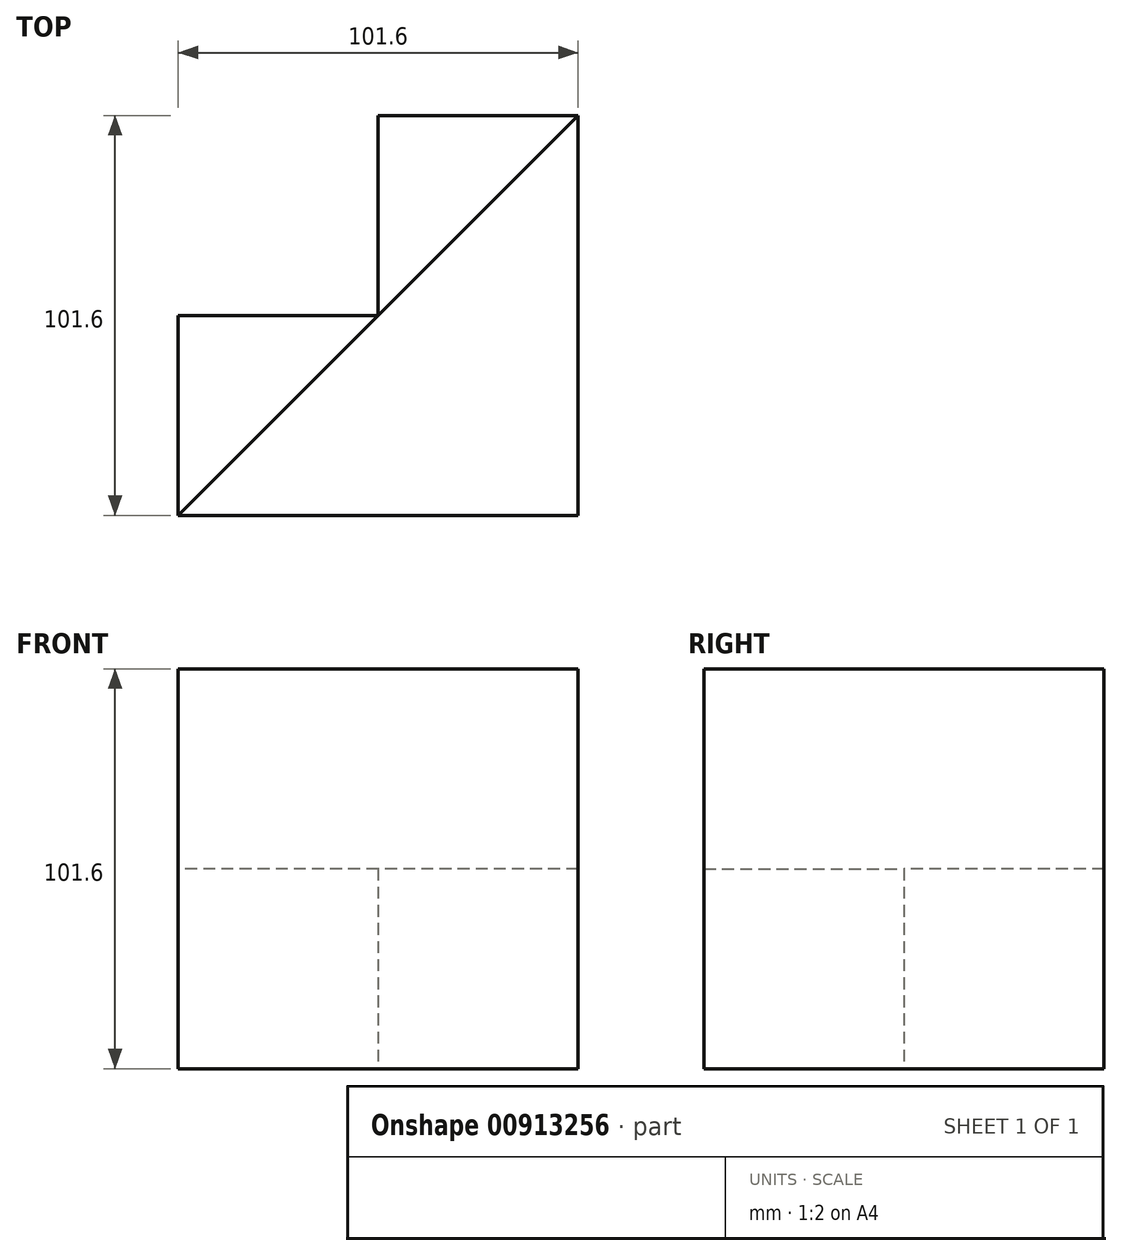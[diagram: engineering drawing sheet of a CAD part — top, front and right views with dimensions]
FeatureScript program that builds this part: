
annotation { "Feature Type Name" : "Feature", "Feature Type Description" : "" }
export const myFeature = defineFeature(function(context is Context, id is Id, definition is map)
    precondition{}
    {
        {
            var Q0;
            Q0=qCreatedBy(makeId("Top.planeOp"),FACE);
            var sketch = newSketch(context, id + "F0", { "sketchPlane" : qUnion([Q0])});
            skLineSegment(sketch, "E0.bottom", {"start": v(0, 0) * mm, "end": v(-101.6, 0) * mm});
            skLineSegment(sketch, "E0.top", {"start": v(0, 101.6) * mm, "end": v(-101.6, 101.6) * mm});
            skLineSegment(sketch, "E0.left", {"start": v(0, 0) * mm, "end": v(0, 101.6) * mm});
            skLineSegment(sketch, "E0.right", {"start": v(-101.6, 0) * mm, "end": v(-101.6, 101.6) * mm});
            skLineSegment(sketch, "E1", {"start": v(0, 101.6) * mm, "end": v(-101.6, 0) * mm});
            skSolve(sketch);
        }
        {
            var Q0;
            Q0=makeQuery(id+"F0.imprint","IMPRINT",FACE,{"disambiguationData":[TD([[makeQuery(id+"F0.imprint","IMPRINT",EDGE,{"derivedFrom":sQuery(id+"F0.wireOp",EDGE,"E0.bottom")}),-1.0]])]});
            extrude(context, id + "F1", {"entities" : qUnion([Q0]), "depth" : 101.6 * mm, "offsetDistance" : 25.4 * mm});
        }
        {
            var Q0;
            Q0=qCreatedBy(makeId("Top.planeOp"),FACE);
            var sketch = newSketch(context, id + "F2", { "sketchPlane" : qUnion([Q0])});
            skLineSegment(sketch, "E2.bottom", {"start": v(0, 0) * mm, "end": v(-101.6, 0) * mm});
            skLineSegment(sketch, "E2.top", {"start": v(0, 101.6) * mm, "end": v(-101.6, 101.6) * mm});
            skLineSegment(sketch, "E2.left", {"start": v(0, 0) * mm, "end": v(0, 101.6) * mm});
            skLineSegment(sketch, "E2.right", {"start": v(-101.6, 0) * mm, "end": v(-101.6, 101.6) * mm});
            skSolve(sketch);
        }
        {
            var Q0;
            Q0 = qSketchRegion(id + "F2", true);
            extrude(context, id + "F3", {"entities" : qUnion([Q0]), "operationType" : NewBodyOperationType.ADD, "depth" : 50.8 * mm, "offsetDistance" : 25.4 * mm});
        }
        {
            var Q0;
            Q0=makeQuery(id+"F3.boolean.opBoolean","MERGE",FACE,{"derivedFrom":[makeQuery(id+"F1.opExtrude","CAP_FACE",FACE,{"disambiguationData":[OSD([sQuery(id+"F0.wireOp",EDGE,"E0.bottom"),sQuery(id+"F0.wireOp",EDGE,"E0.left"),sQuery(id+"F0.wireOp",EDGE,"E1")])],"isStart":true}),makeQuery(id+"F3.opExtrude","CAP_FACE",FACE,{"disambiguationData":[OSD([sQuery(id+"F2.wireOp",EDGE,"E2.bottom"),sQuery(id+"F2.wireOp",EDGE,"E2.top"),sQuery(id+"F2.wireOp",EDGE,"E2.left"),sQuery(id+"F2.wireOp",EDGE,"E2.right")])],"isStart":true})]});
            var sketch = newSketch(context, id + "F4", { "sketchPlane" : qUnion([Q0])});
            skLineSegment(sketch, "E3.bottom", {"start": v(-101.6, -101.6) * mm, "end": v(-50.8, -101.6) * mm});
            skLineSegment(sketch, "E3.top", {"start": v(-101.6, -50.8) * mm, "end": v(-50.8, -50.8) * mm});
            skLineSegment(sketch, "E3.left", {"start": v(-101.6, -101.6) * mm, "end": v(-101.6, -50.8) * mm});
            skLineSegment(sketch, "E3.right", {"start": v(-50.8, -101.6) * mm, "end": v(-50.8, -50.8) * mm});
            skSolve(sketch);
        }
        {
            var Q0;
            Q0 = qSketchRegion(id + "F4", true);
            extrude(context, id + "F5", {"entities" : qUnion([Q0]), "operationType" : NewBodyOperationType.REMOVE, "endBound" : BoundingType.THROUGH_ALL, "oppositeDirection" : true, "depth" : 25.4 * mm, "offsetDistance" : 25.4 * mm});
        }
    });
